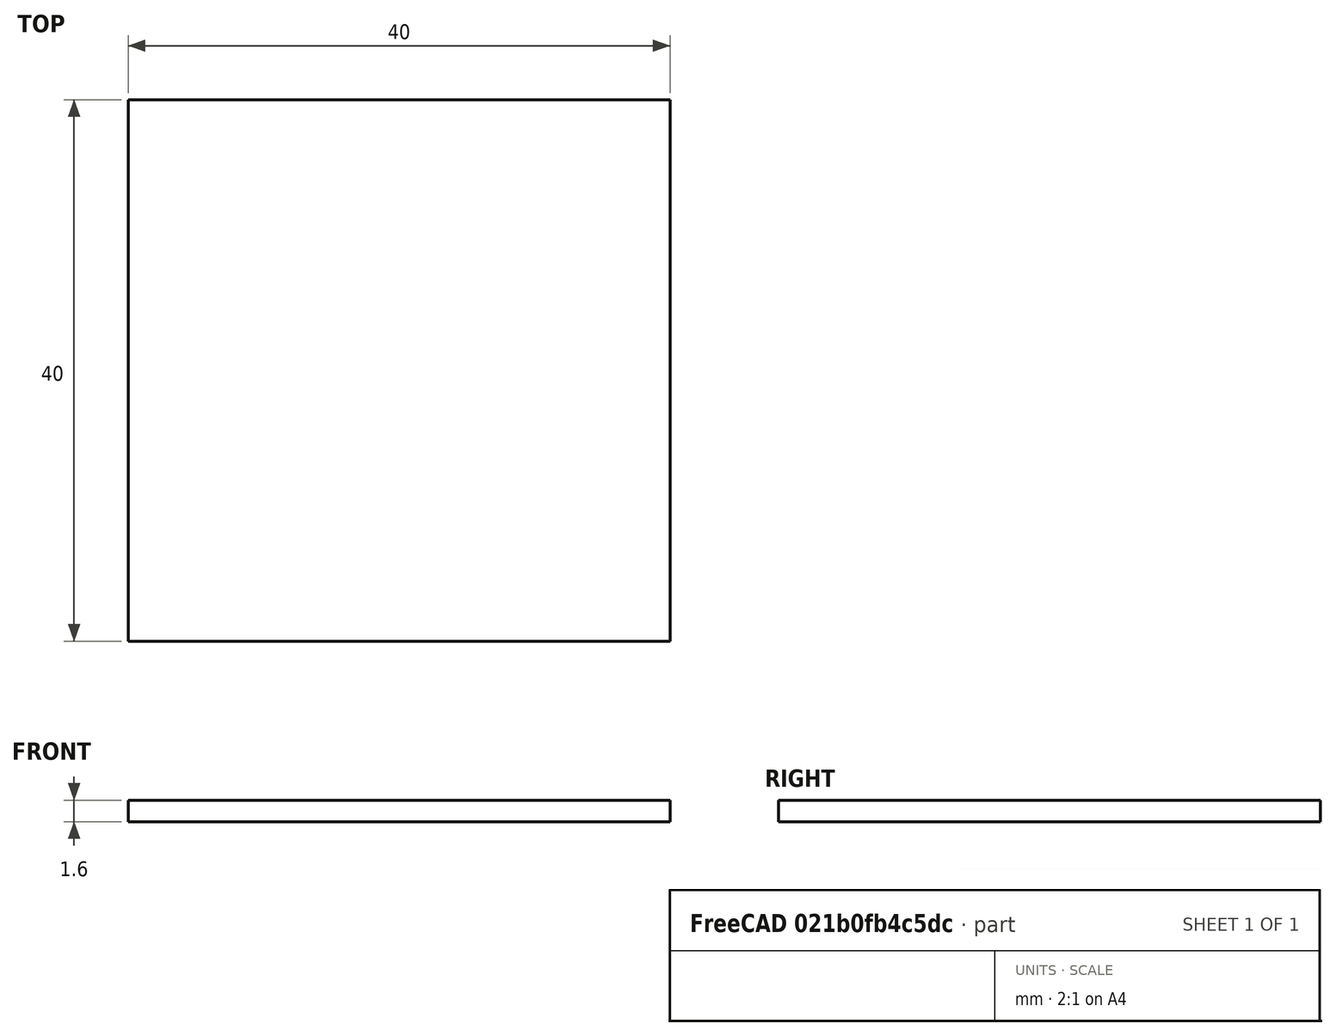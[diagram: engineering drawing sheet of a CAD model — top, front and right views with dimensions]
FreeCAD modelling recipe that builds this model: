
FCSTD DOCUMENT  (FreeCAD 0.19R24291 (Git))
Label: Top-To-PCB
License: All rights reserved
LicenseURL: http://en.wikipedia.org/wiki/All_rights_reserved
objects: Mesh::Feature×1, Sketcher::SketchObject×1, PartDesign::Pad×1, PartDesign::Body×1
note: 4 computed .brp shape members not serialized (recipe doc carries the construction recipe); baked Part::Feature solids carry a one-line shape summary decoded from their .brp

FEATURE [Mesh::Feature] Top
  Placement = pos=(21.5,4.6,-18.7) rot=(0,0,1;0rad)
FEATURE [Sketcher::SketchObject] Sketch  label="dessin-pcb"
  FullyConstrained = false
  MapMode = 5
  Support = -> [XY_Plane]
  sketch-geometry (4):
    g0: LineSegment StartX=1.20852 StartY=1.77821 StartZ=0 EndX=41.2085 EndY=1.77821 EndZ=0
    g1: LineSegment StartX=41.2085 StartY=1.77821 StartZ=0 EndX=41.2085 EndY=41.7782 EndZ=0
    g2: LineSegment StartX=41.2085 StartY=41.7782 StartZ=0 EndX=1.20852 EndY=41.7782 EndZ=0
    g3: LineSegment StartX=1.20852 StartY=41.7782 StartZ=0 EndX=1.20852 EndY=1.77821 EndZ=0
  constraints (10):
    c: Coincident(g0,g1)
    c: Coincident(g1,g2)
    c: Coincident(g2,g3)
    c: Coincident(g3,g0)
    c: Horizontal(g0)
    c: Horizontal(g2)
    c: Vertical(g1)
    c: Vertical(g3)
    c: DistanceY(g3,g3) = 40
    c: DistanceX(g2,g2) = 40
FEATURE [PartDesign::Pad] Pad
  Direction = (1,1,1)
  Length = 1.6
  Length2 = 100
  Profile = -> Sketch
  Type = 0
FEATURE [PartDesign::Body] Body  label="PCB"
  Group = -> [Sketch,Pad]
  Origin = -> Origin
  Tip = -> Pad
